AUTODESK INVENTOR PART (.ipt)
format: ipt  version: 2024 (Build 280153000, 153)  size: 263,680 bytes
history: native  units: in
note: dims shown in document units (in); Inventor stores cm internally (conversion verified against a paired STEP export)
features: sketch x2, extrude x2, hole x1
ambient origin geometry x8: Origin, YZ Plane, XZ Plane, XY Plane, X Axis, Y Axis, Z Axis, Center Point
bodies: Solid1 (feature_tree)
feature tree (5):
  sketch  "Sketch2"  dims[d3=0.5in d4=1.25in]
  extrude  "Extrusion1"  Depth=0.5in
  hole  "Hole3"  [1 undecoded]
  extrude  "Extrusion2"  Depth=0.0625in TaperAngle=0.0deg
  sketch  "Sketch3"  dims[d5=0.5in d6=0.875in d8=0.0625in d9=0.0in d18=0.125in d19=0.0625in d23=0.185in d24=0.5in d25=1.0in d26=3.0in d27=2.0in d28=0.125in d33=0.25in d35=0.25in d36=0.25in d37=0.25in d38=0.5in d46=0.1875in d47=0.75in d48=0.375in d49=0.25in d50=0.5635in d51=1.0in d52=0.8108in d54=0.25in d55=1.0in d56=2.0in d58=0.75in d59=0.125in d60=0.5in d61=1.25in d62=1.0in d63=0.7518in d64=180.0deg d65=2.0in d66=90.0deg d69=0.055in d70=0.75in d71=90.0deg d72=0.25in d73=0.5in d77=0.375in d78=0.25in d79=0.0104in d80=0.0in d81=0.0in]
note: 1 required parameter value undecoded (feature->parameter linkage not recoverable at this tier; creation-order binding heuristic only, values carry confidence <= 0.55)
